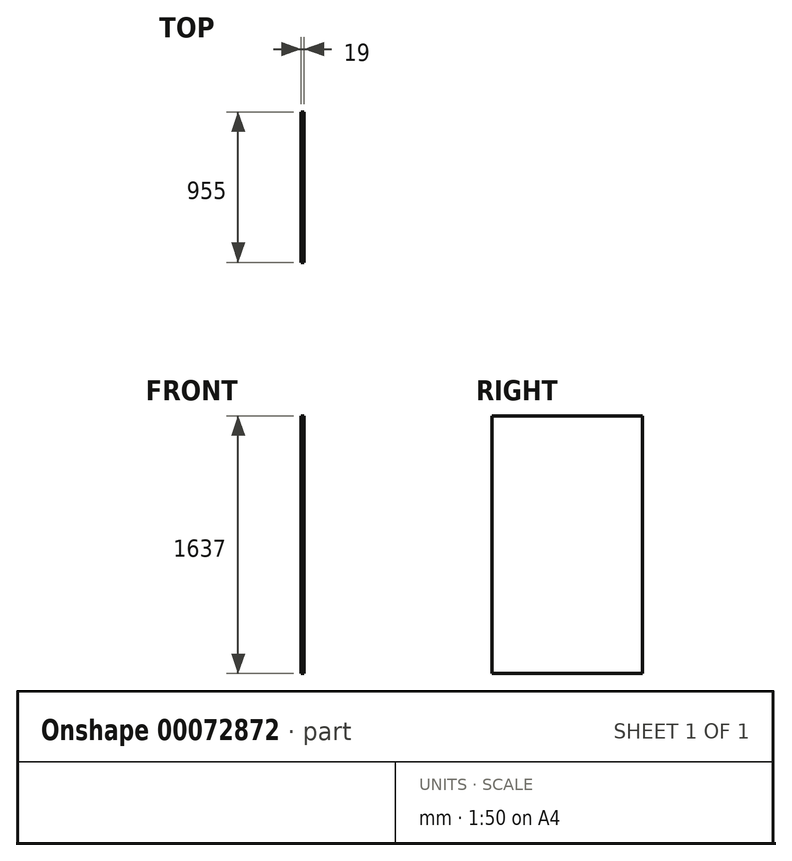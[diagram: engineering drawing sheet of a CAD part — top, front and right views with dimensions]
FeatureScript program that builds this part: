
annotation { "Feature Type Name" : "Feature", "Feature Type Description" : "" }
export const myFeature = defineFeature(function(context is Context, id is Id, definition is map)
    precondition{}
    {
        {
            var Q0;
            Q0=qCreatedBy(makeId("Right.planeOp"),FACE);
            var sketch = newSketch(context, id + "F0", { "sketchPlane" : qUnion([Q0])});
            skLineSegment(sketch, "E0.bottom", {"start": v(0, 0) * mm, "end": v(955, 0) * mm});
            skLineSegment(sketch, "E0.top", {"start": v(0, -1637) * mm, "end": v(955, -1637) * mm});
            skLineSegment(sketch, "E0.left", {"start": v(0, 0) * mm, "end": v(0, -1637) * mm});
            skLineSegment(sketch, "E0.right", {"start": v(955, 0) * mm, "end": v(955, -1637) * mm});
            skSolve(sketch);
        }
        {
            var Q0;
            Q0=makeQuery(id+"F0.imprint","IMPRINT",FACE,{"disambiguationData":[TD([[makeQuery(id+"F0.imprint","IMPRINT",EDGE,{"derivedFrom":sQuery(id+"F0.wireOp",EDGE,"E0.bottom")}),-1.0]])]});
            extrude(context, id + "F1", {"entities" : qUnion([Q0]), "depth" : 19 * mm});
        }
    });
